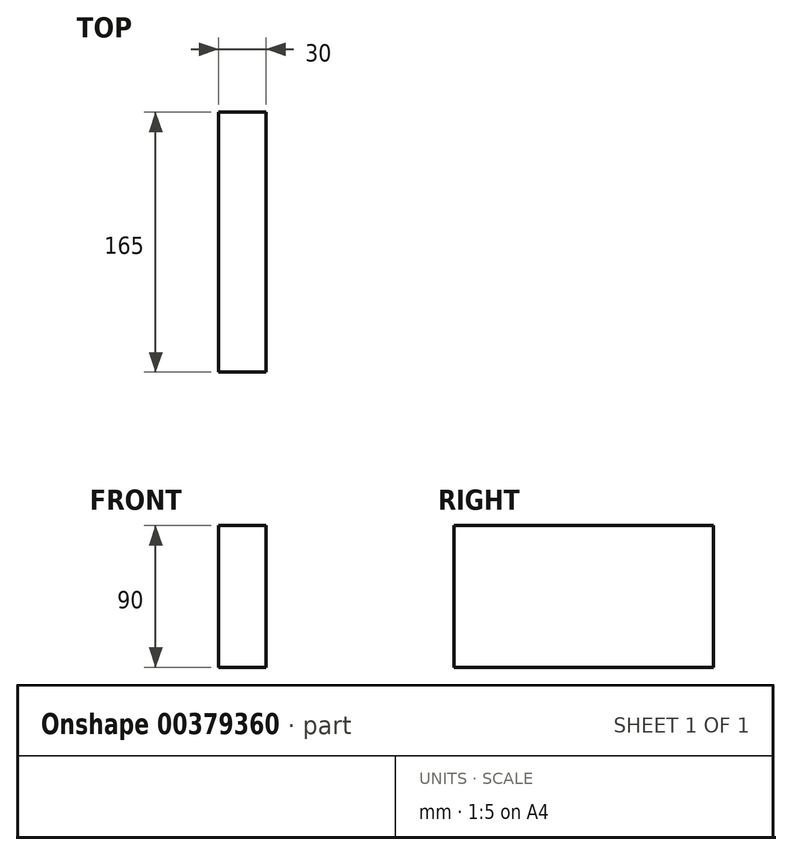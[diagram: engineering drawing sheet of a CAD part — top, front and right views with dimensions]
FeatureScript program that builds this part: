
annotation { "Feature Type Name" : "Feature", "Feature Type Description" : "" }
export const myFeature = defineFeature(function(context is Context, id is Id, definition is map)
    precondition{}
    {
        {
            var Q0;
            Q0=qCreatedBy(makeId("Right.planeOp"),FACE);
            var sketch = newSketch(context, id + "F0", { "sketchPlane" : qUnion([Q0])});
            skLineSegment(sketch, "E0.bottom", {"start": v(-76.08, 73.26) * mm, "end": v(88.92, 73.26) * mm});
            skLineSegment(sketch, "E0.top", {"start": v(-76.08, -16.74) * mm, "end": v(88.92, -16.74) * mm});
            skLineSegment(sketch, "E0.left", {"start": v(-76.08, 73.26) * mm, "end": v(-76.08, -16.74) * mm});
            skLineSegment(sketch, "E0.right", {"start": v(88.92, 73.26) * mm, "end": v(88.92, -16.74) * mm});
            skSolve(sketch);
        }
        {
            var Q0;
            Q0=makeQuery(id+"F0.imprint","IMPRINT",FACE,{"disambiguationData":[TD([[makeQuery(id+"F0.imprint","IMPRINT",EDGE,{"derivedFrom":sQuery(id+"F0.wireOp",EDGE,"E0.bottom")}),-1.0]])]});
            extrude(context, id + "F1", {"entities" : qUnion([Q0]), "depth" : 30 * mm, "offsetDistance" : 25 * mm});
        }
    });
